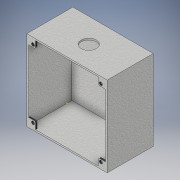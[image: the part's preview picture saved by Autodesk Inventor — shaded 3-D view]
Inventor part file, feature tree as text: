
AUTODESK INVENTOR PART (.ipt)
format: ipt  version: 2018 (Build 220112000, 112)  size: 205,824 bytes
history: native  units: in
note: dims shown in document units (in); Inventor stores cm internally (conversion verified against a paired STEP export)
features: sketch x5, extrude x4, fillet x1
ambient origin geometry x8: Origin, YZ Plane, XZ Plane, XY Plane, X Axis, Y Axis, Z Axis, Center Point
bodies: Solid1 (feature_tree)
feature tree (10):
  extrude  "Extrusion1"  Depth=4.0in
  extrude  "Extrusion2"  Depth=0.08in
  extrude  "Extrusion3"  Depth=2.1654in TaperAngle=0.0deg
  sketch  "Sketch6"  dims[d9=0.75in d10=1.0in d11=0.0in d12=3.375in]
  extrude  "Extrusion4"  Depth=1.0in TaperAngle=0.0deg
  fillet  "Fillet1"  Radius=3.375in
  sketch  "Sketch1"  dims[d0=4.0in d1=4.0in]
  sketch  "Sketch2"  dims[d2=0.125in d3=0.0in d4=0.08in]
  sketch  "Sketch5"  dims[d5=0.08in d6=2.1654in d7=0.0in]
  sketch  "Sketch7"  dims[d13=0.1575in d14=0.1575in d16=3.375in d17=1.6875in d18=1.6875in d19=0.1575in d20=0.1575in d21=1.6875in d22=1.6875in d23=3.375in d24=1.6875in d25=1.6875in d26=0.125in d27=0.125in d28=0.125in d29=0.125in d30=0.125in d31=0.125in d32=0.125in d33=0.125in d34=0.0787in d35=0.0in d36=0.0787in]
